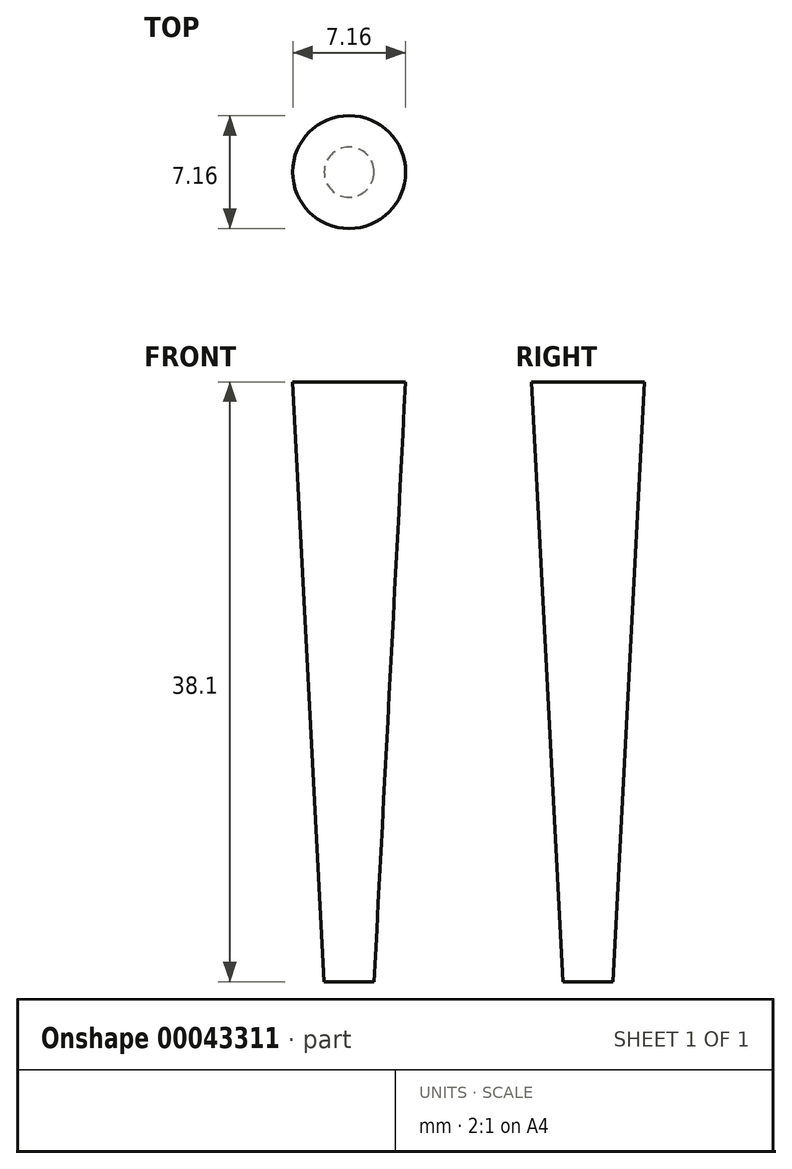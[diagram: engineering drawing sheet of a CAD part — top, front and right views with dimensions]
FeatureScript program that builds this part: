
annotation { "Feature Type Name" : "Feature", "Feature Type Description" : "" }
export const myFeature = defineFeature(function(context is Context, id is Id, definition is map)
    precondition{}
    {
        {
            var Q0;
            Q0=qCreatedBy(makeId("Top.planeOp"),FACE);
            var sketch = newSketch(context, id + "F0", { "sketchPlane" : qUnion([Q0])});
            skCircle(sketch, "E0", {"center": v(0, 0) * mm, "radius": 1.59 * mm});
            skSolve(sketch);
        }
        {
            var Q0;
            Q0=makeQuery(id+"F0.imprint","IMPRINT",FACE,{"disambiguationData":[TD([[makeQuery(id+"F0.imprint","IMPRINT",EDGE,{"derivedFrom":sQuery(id+"F0.wireOp",EDGE,"E0")}),1.0]])]});
            extrude(context, id + "F1", {"entities" : qUnion([Q0]), "depth" : 38.1 * mm, "hasDraft" : true, "draftAngle" : 3 * degree});
        }
    });
